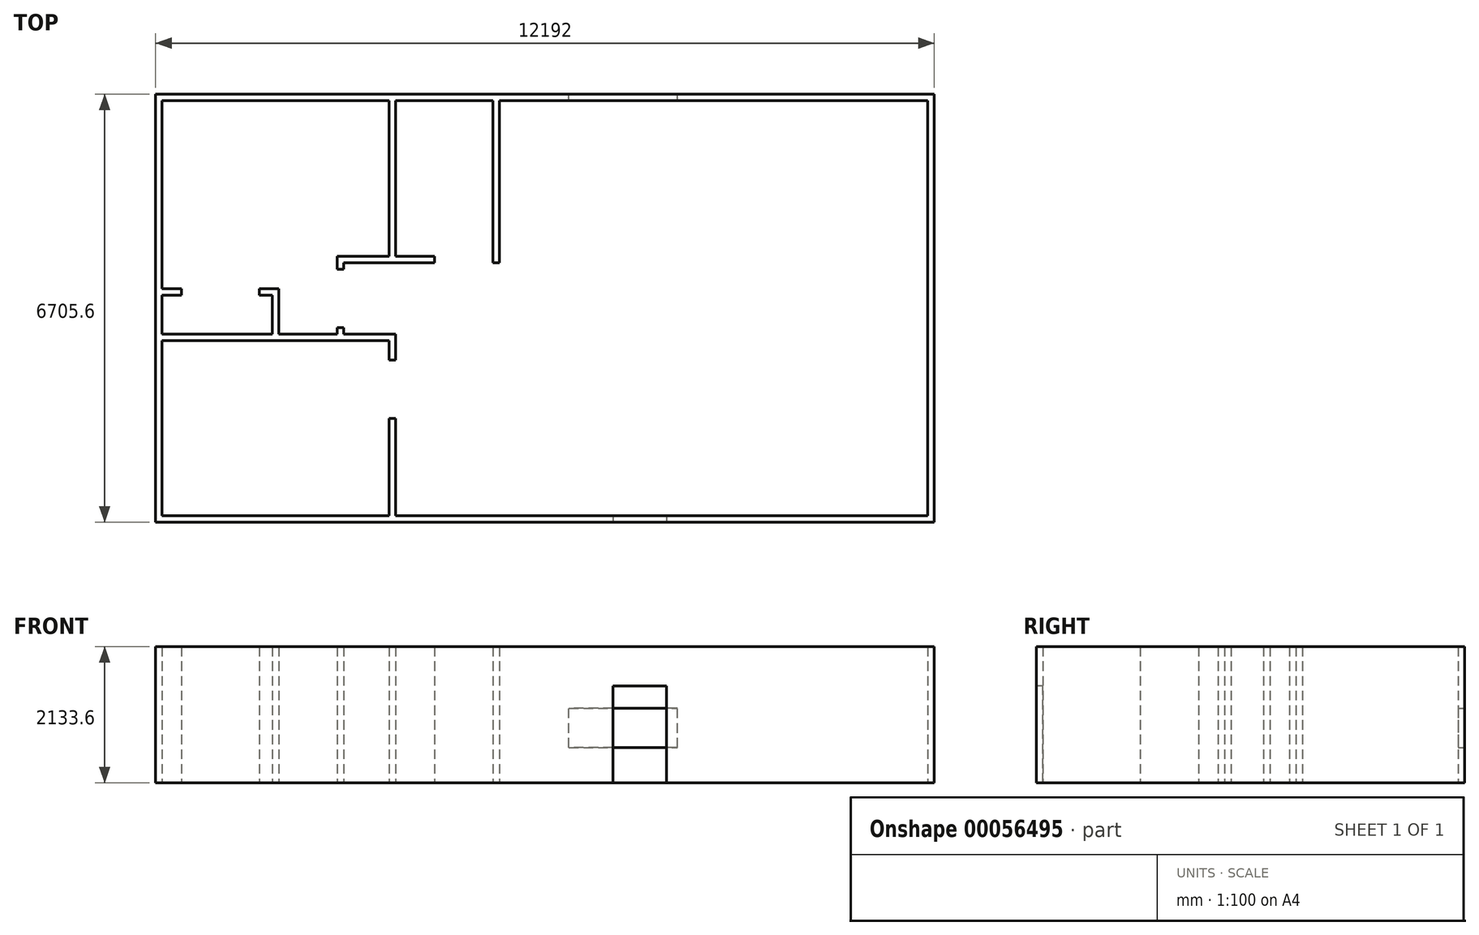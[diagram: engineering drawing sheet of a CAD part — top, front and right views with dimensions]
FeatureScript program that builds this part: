
annotation { "Feature Type Name" : "Feature", "Feature Type Description" : "" }
export const myFeature = defineFeature(function(context is Context, id is Id, definition is map)
    precondition{}
    {
        {
            var Q0;
            Q0=qCreatedBy(makeId("Top.planeOp"),FACE);
            var sketch = newSketch(context, id + "F0", { "sketchPlane" : qUnion([Q0])});
            skLineSegment(sketch, "E0.bottom", {"start": v(-6096, 3810) * mm, "end": v(6096, 3810) * mm});
            skLineSegment(sketch, "E0.top", {"start": v(-6096, -2895.6) * mm, "end": v(6096, -2895.6) * mm});
            skLineSegment(sketch, "E0.left", {"start": v(-6096, 3810) * mm, "end": v(-6096, -2895.6) * mm});
            skLineSegment(sketch, "E0.right", {"start": v(6096, 3810) * mm, "end": v(6096, -2895.6) * mm});
            skLineSegment(sketch, "E1.0", {"start": v(-5994.4, 3708.4) * mm, "end": v(-2438.4, 3708.4) * mm});
            skLineSegment(sketch, "E1.1", {"start": v(-5994.4, 3708.4) * mm, "end": v(-5994.4, 762) * mm});
            skLineSegment(sketch, "E1.2", {"start": v(-5994.4, -2794) * mm, "end": v(-2438.4, -2794) * mm});
            skLineSegment(sketch, "E1.3", {"start": v(5994.4, 3708.4) * mm, "end": v(5994.4, -2794) * mm});
            skLineSegment(sketch, "E2.right", {"start": v(-2336.8, 3708.4) * mm, "end": v(-2336.8, 1270) * mm});
            skLineSegment(sketch, "E3.top", {"start": v(-5994.4, 50.8) * mm, "end": v(-4267.2, 50.8) * mm});
            skLineSegment(sketch, "E3.left", {"start": v(-5994.4, -2794) * mm, "end": v(-5994.4, -50.8) * mm});
            skLineSegment(sketch, "E3.right", {"start": v(-2336.8, -2794) * mm, "end": v(-2336.8, -1270) * mm});
            skLineSegment(sketch, "E4.0", {"start": v(-3251.2, 1270) * mm, "end": v(-2438.4, 1270) * mm});
            skLineSegment(sketch, "E4.1", {"start": v(-2438.4, 3708.4) * mm, "end": v(-2438.4, 1270) * mm});
            skLineSegment(sketch, "E5.0", {"start": v(-2438.4, -2794) * mm, "end": v(-2438.4, -1270) * mm});
            skLineSegment(sketch, "E5.1", {"start": v(-5994.4, -50.8) * mm, "end": v(-2438.4, -50.8) * mm});
            skLineSegment(sketch, "E6", {"start": v(-3149.6, 1168.4) * mm, "end": v(-3149.6, 1066.8) * mm});
            skLineSegment(sketch, "E7.trimOffspring", {"start": v(-2336.8, -2794) * mm, "end": v(5994.4, -2794) * mm});
            skLineSegment(sketch, "E8.trimOffspring", {"start": v(-5994.4, -50.8) * mm, "end": v(-5994.4, -2794) * mm});
            skLineSegment(sketch, "E9.trimOffspring", {"start": v(-3149.6, 1168.4) * mm, "end": v(-2336.8, 1168.4) * mm});
            skLineSegment(sketch, "E10.trimOffspring", {"start": v(-3149.6, 50.8) * mm, "end": v(-2336.8, 50.8) * mm});
            skLineSegment(sketch, "E11", {"start": v(-3251.2, 152.4) * mm, "end": v(-3149.6, 152.4) * mm});
            skLineSegment(sketch, "E12", {"start": v(-3251.2, 1066.8) * mm, "end": v(-3149.6, 1066.8) * mm});
            skLineSegment(sketch, "E13.trimOffspring", {"start": v(-3251.2, 152.4) * mm, "end": v(-3251.2, 50.8) * mm});
            skLineSegment(sketch, "E14.trimOffspring", {"start": v(-3149.6, 152.4) * mm, "end": v(-3149.6, 50.8) * mm});
            skLineSegment(sketch, "E15", {"start": v(-3251.2, 1270) * mm, "end": v(-3251.2, 1066.8) * mm});
            skLineSegment(sketch, "E16", {"start": v(-2438.4, -355.6) * mm, "end": v(-2336.8, -355.6) * mm});
            skLineSegment(sketch, "E17", {"start": v(-2438.4, -1270) * mm, "end": v(-2336.8, -1270) * mm});
            skLineSegment(sketch, "E18.trimOffspring", {"start": v(-2438.4, -355.6) * mm, "end": v(-2438.4, -50.8) * mm});
            skLineSegment(sketch, "E19.trimOffspring", {"start": v(-2336.8, -355.6) * mm, "end": v(-2336.8, 50.8) * mm});
            skLineSegment(sketch, "E20", {"start": v(-5994.4, 762) * mm, "end": v(-5689.6, 762) * mm});
            skLineSegment(sketch, "E21", {"start": v(-5689.6, 762) * mm, "end": v(-5689.6, 660.4) * mm});
            skLineSegment(sketch, "E22", {"start": v(-5689.6, 660.4) * mm, "end": v(-5994.4, 660.4) * mm});
            skLineSegment(sketch, "E23.trimOffspring", {"start": v(-5994.4, 660.4) * mm, "end": v(-5994.4, 50.8) * mm});
            skLineSegment(sketch, "E24", {"start": v(-4267.2, 50.8) * mm, "end": v(-4267.2, 660.4) * mm});
            skLineSegment(sketch, "E25", {"start": v(-4267.2, 660.4) * mm, "end": v(-4470.4, 660.4) * mm});
            skLineSegment(sketch, "E26", {"start": v(-4470.4, 762) * mm, "end": v(-4470.4, 660.4) * mm});
            skLineSegment(sketch, "E27", {"start": v(-4470.4, 762) * mm, "end": v(-4165.6, 762) * mm});
            skLineSegment(sketch, "E28", {"start": v(-4165.6, 762) * mm, "end": v(-4165.6, 50.8) * mm});
            skLineSegment(sketch, "E29.trimOffspring", {"start": v(-4165.6, 50.8) * mm, "end": v(-3251.2, 50.8) * mm});
            skLineSegment(sketch, "E30.trimOffspring", {"start": v(-2336.8, 3708.4) * mm, "end": v(-812.8, 3708.4) * mm});
            skLineSegment(sketch, "E31", {"start": v(-711.2, 3708.4) * mm, "end": v(-711.2, 1168.4) * mm});
            skLineSegment(sketch, "E32", {"start": v(-711.2, 1168.4) * mm, "end": v(-812.8, 1168.4) * mm});
            skLineSegment(sketch, "E33", {"start": v(-812.8, 1168.4) * mm, "end": v(-812.8, 3708.4) * mm});
            skLineSegment(sketch, "E34", {"start": v(-2336.8, 1168.4) * mm, "end": v(-1727.2, 1168.4) * mm});
            skLineSegment(sketch, "E35", {"start": v(-1727.2, 1168.4) * mm, "end": v(-1727.2, 1270) * mm});
            skLineSegment(sketch, "E36", {"start": v(-2336.8, 1270) * mm, "end": v(-1727.2, 1270) * mm});
            skLineSegment(sketch, "E37.trimOffspring", {"start": v(-711.2, 3708.4) * mm, "end": v(5994.4, 3708.4) * mm});
            skSolve(sketch);
        }
        {
            var Q0;
            Q0=makeQuery(id+"F0.imprint","IMPRINT",FACE,{"disambiguationData":[TD([[makeQuery(id+"F0.imprint","IMPRINT",EDGE,{"derivedFrom":sQuery(id+"F0.wireOp",EDGE,"E0.bottom")}),-1.0]])]});
            extrude(context, id + "F1", {"entities" : qUnion([Q0]), "depth" : 2133.6 * mm});
        }
        {
            var Q0;
            Q0=makeQuery(id+"F1.opExtrude","SWEPT_FACE",FACE,{"disambiguationData":[OSD([sQuery(id+"F0.wireOp",EDGE,"E0.top")])]});
            var sketch = newSketch(context, id + "F2", { "sketchPlane" : qUnion([Q0])});
            skLineSegment(sketch, "E38.bottom", {"start": v(1062.43, 0) * mm, "end": v(1901.88, 0) * mm});
            skLineSegment(sketch, "E38.top", {"start": v(1062.43, 1520.56) * mm, "end": v(1901.88, 1520.56) * mm});
            skLineSegment(sketch, "E38.left", {"start": v(1062.43, 0) * mm, "end": v(1062.43, 1520.56) * mm});
            skLineSegment(sketch, "E38.right", {"start": v(1901.88, 0) * mm, "end": v(1901.88, 1520.56) * mm});
            skSolve(sketch);
        }
        {
            var Q0;
            Q0=makeQuery(id+"F2.imprint","IMPRINT",FACE,{"disambiguationData":[TD([[makeQuery(id+"F2.imprint","IMPRINT",EDGE,{"derivedFrom":sQuery(id+"F2.wireOp",EDGE,"E38.bottom")}),1.0]])]});
            extrude(context, id + "F3", {"entities" : qUnion([Q0]), "operationType" : NewBodyOperationType.REMOVE, "endBound" : BoundingType.UP_TO_NEXT, "oppositeDirection" : true, "depth" : 25.4 * mm});
        }
        {
            var Q0;
            Q0=makeQuery(id+"F1.opExtrude","SWEPT_FACE",FACE,{"disambiguationData":[OSD([sQuery(id+"F0.wireOp",EDGE,"E0.bottom")])]});
            var sketch = newSketch(context, id + "F4", { "sketchPlane" : qUnion([Q0])});
            skLineSegment(sketch, "E39.bottom", {"start": v(-374.09, 554.4) * mm, "end": v(-2070.85, 554.4) * mm});
            skLineSegment(sketch, "E39.top", {"start": v(-374.09, 1168.98) * mm, "end": v(-2070.85, 1168.98) * mm});
            skLineSegment(sketch, "E39.left", {"start": v(-374.09, 554.4) * mm, "end": v(-374.09, 1168.98) * mm});
            skLineSegment(sketch, "E39.right", {"start": v(-2070.85, 554.4) * mm, "end": v(-2070.85, 1168.98) * mm});
            skSolve(sketch);
        }
        {
            var Q0;
            Q0=makeQuery(id+"F4.imprint","IMPRINT",FACE,{"disambiguationData":[TD([[makeQuery(id+"F4.imprint","IMPRINT",EDGE,{"derivedFrom":sQuery(id+"F4.wireOp",EDGE,"E39.bottom")}),-1.0]])]});
            extrude(context, id + "F5", {"entities" : qUnion([Q0]), "operationType" : NewBodyOperationType.REMOVE, "endBound" : BoundingType.UP_TO_NEXT, "oppositeDirection" : true, "depth" : 25.4 * mm});
        }
    });
